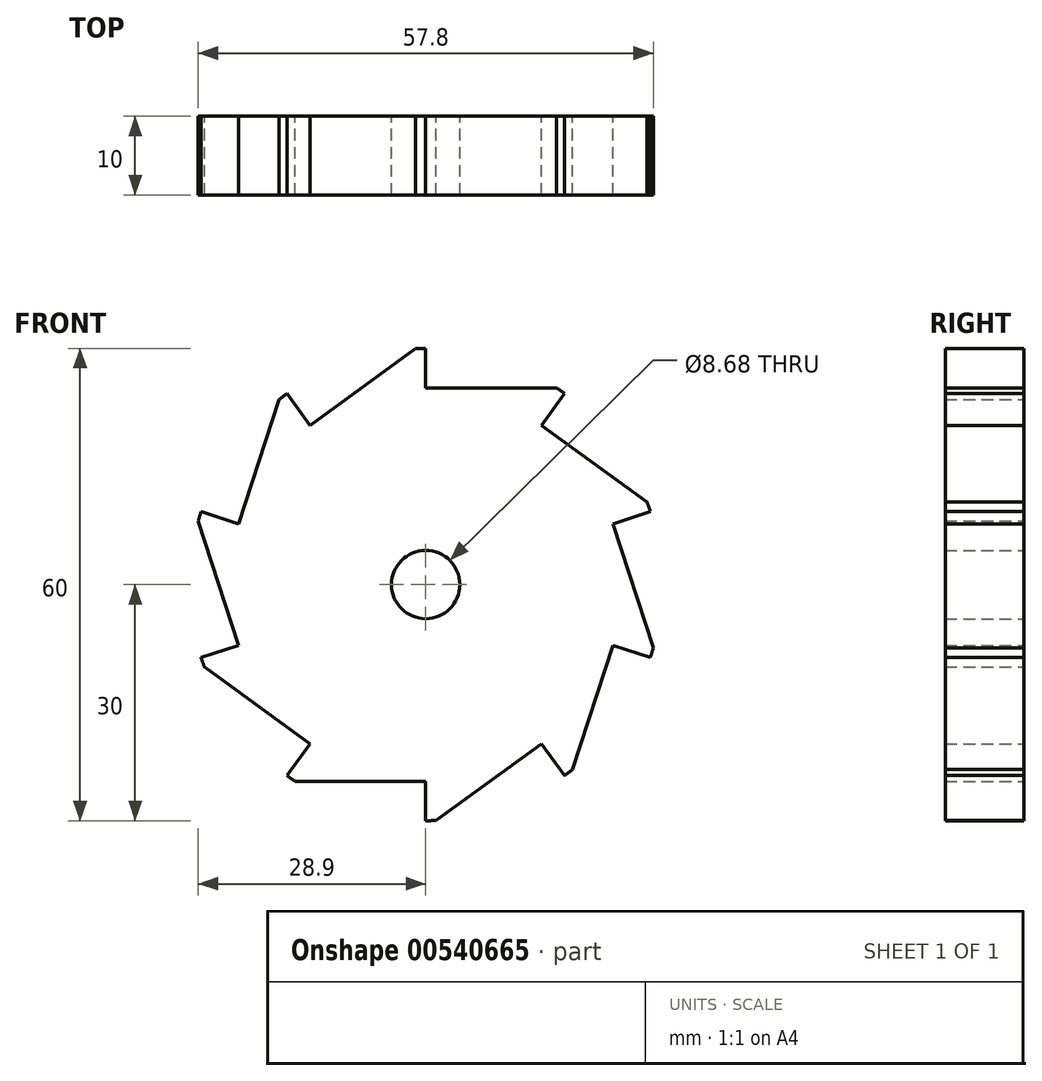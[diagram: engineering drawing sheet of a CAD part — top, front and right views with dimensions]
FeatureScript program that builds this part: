
annotation { "Feature Type Name" : "Feature", "Feature Type Description" : "" }
export const myFeature = defineFeature(function(context is Context, id is Id, definition is map)
    precondition{}
    {
        {
            var Q0;
            Q0=qCreatedBy(makeId("Front.planeOp"),FACE);
            var sketch = newSketch(context, id + "F0", { "sketchPlane" : qUnion([Q0])});
            skArc(sketch, "E0", {"start": v(17.63, 24.27) * mm, "mid": v(17.11, 24.64) * mm, "end": v(16.58, 25) * mm});
            skLineSegment(sketch, "E1", {"start": v(0, 30) * mm, "end": v(0, 25) * mm});
            skLineSegment(sketch, "E2", {"start": v(0, 25) * mm, "end": v(16.58, 25) * mm});
            skLineSegment(sketch, "E3.1.0", {"start": v(-17.63, 24.27) * mm, "end": v(-14.7, 20.23) * mm});
            skLineSegment(sketch, "E3.1.1", {"start": v(-14.7, 20.23) * mm, "end": v(-1.28, 29.97) * mm});
            skLineSegment(sketch, "E3.2.0", {"start": v(-28.53, 9.27) * mm, "end": v(-23.78, 7.73) * mm});
            skLineSegment(sketch, "E3.2.1", {"start": v(-23.78, 7.73) * mm, "end": v(-18.65, 23.5) * mm});
            skLineSegment(sketch, "E4.2.3.0", {"start": v(-28.53, -9.27) * mm, "end": v(-23.78, -7.73) * mm});
            skLineSegment(sketch, "E4.3.3.0", {"start": v(-23.78, -7.73) * mm, "end": v(-28.9, 8.05) * mm});
            skLineSegment(sketch, "E4.2.4.0", {"start": v(-17.63, -24.27) * mm, "end": v(-14.7, -20.23) * mm});
            skLineSegment(sketch, "E4.3.4.0", {"start": v(-14.7, -20.23) * mm, "end": v(-28.11, -10.48) * mm});
            skLineSegment(sketch, "E4.2.5.0", {"start": v(0, -30) * mm, "end": v(0, -25) * mm});
            skLineSegment(sketch, "E4.3.5.0", {"start": v(0, -25) * mm, "end": v(-16.58, -25) * mm});
            skLineSegment(sketch, "E4.2.6.0", {"start": v(17.63, -24.27) * mm, "end": v(14.7, -20.23) * mm});
            skLineSegment(sketch, "E4.3.6.0", {"start": v(14.7, -20.23) * mm, "end": v(1.28, -29.97) * mm});
            skLineSegment(sketch, "E4.2.7.0", {"start": v(28.53, -9.27) * mm, "end": v(23.78, -7.73) * mm});
            skLineSegment(sketch, "E4.3.7.0", {"start": v(23.78, -7.73) * mm, "end": v(18.65, -23.5) * mm});
            skLineSegment(sketch, "E4.2.8.0", {"start": v(28.53, 9.27) * mm, "end": v(23.78, 7.73) * mm});
            skLineSegment(sketch, "E4.3.8.0", {"start": v(23.78, 7.73) * mm, "end": v(28.9, -8.05) * mm});
            skLineSegment(sketch, "E4.2.9.0", {"start": v(17.63, 24.27) * mm, "end": v(14.7, 20.23) * mm});
            skLineSegment(sketch, "E4.3.9.0", {"start": v(14.7, 20.23) * mm, "end": v(28.11, 10.48) * mm});
            skArc(sketch, "E5.trimOffspring", {"start": v(0, 30) * mm, "mid": v(-0.64, 30) * mm, "end": v(-1.28, 29.97) * mm});
            skArc(sketch, "E6.trimOffspring", {"start": v(-17.63, 24.27) * mm, "mid": v(-18.15, 23.89) * mm, "end": v(-18.65, 23.5) * mm});
            skArc(sketch, "E7.trimOffspring", {"start": v(-28.53, 9.27) * mm, "mid": v(-28.72, 8.66) * mm, "end": v(-28.9, 8.05) * mm});
            skArc(sketch, "E8.trimOffspring", {"start": v(28.53, 9.27) * mm, "mid": v(28.33, 9.88) * mm, "end": v(28.11, 10.48) * mm});
            skArc(sketch, "E9.trimOffspring", {"start": v(28.53, -9.27) * mm, "mid": v(28.72, -8.66) * mm, "end": v(28.9, -8.05) * mm});
            skArc(sketch, "E10.trimOffspring", {"start": v(17.63, -24.27) * mm, "mid": v(18.15, -23.89) * mm, "end": v(18.65, -23.5) * mm});
            skArc(sketch, "E11.trimOffspring", {"start": v(0, -30) * mm, "mid": v(0.64, -30) * mm, "end": v(1.28, -29.97) * mm});
            skArc(sketch, "E12.trimOffspring", {"start": v(-17.63, -24.27) * mm, "mid": v(-17.11, -24.64) * mm, "end": v(-16.58, -25) * mm});
            skArc(sketch, "E13.trimOffspring", {"start": v(-28.53, -9.27) * mm, "mid": v(-28.33, -9.88) * mm, "end": v(-28.11, -10.48) * mm});
            skSolve(sketch);
        }
        {
            var Q0;
            Q0=makeQuery(id+"F0.imprint","IMPRINT",FACE,{"disambiguationData":[TD([[makeQuery(id+"F0.imprint","IMPRINT",EDGE,{"derivedFrom":sQuery(id+"F0.wireOp",EDGE,"E0")}),1.0]])]});
            extrude(context, id + "F1", {"entities" : qUnion([Q0]), "depth" : 10 * mm, "offsetDistance" : 25 * mm});
        }
        {
            var Q0;
            Q0=qCreatedBy(makeId("Front.planeOp"),FACE);
            var sketch = newSketch(context, id + "F2", { "sketchPlane" : qUnion([Q0])});
            skCircle(sketch, "E14", {"center": v(0, 0) * mm, "radius": 4.34 * mm});
            skSolve(sketch);
        }
        {
            var Q0;
            Q0 = qSketchRegion(id + "F2", true);
            extrude(context, id + "F3", {"entities" : qUnion([Q0]), "operationType" : NewBodyOperationType.REMOVE, "depth" : 25 * mm, "offsetDistance" : 25 * mm});
        }
    });
